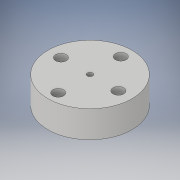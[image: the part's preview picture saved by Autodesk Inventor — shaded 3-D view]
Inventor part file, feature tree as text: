
AUTODESK INVENTOR PART (.ipt)
format: ipt  version: 2019 (Build 230136000, 136)  size: 108,544 bytes
history: native  units: mm
features: extrude x1, sketch x1
ambient origin geometry x8: Origin, YZ Plane, XZ Plane, XY Plane, X Axis, Y Axis, Z Axis, Center Point
bodies: Solid1 (feature_tree)
feature tree (2):
  extrude  "Extrusion1"  Depth=5.0mm
  sketch  "Sketch1"  dims[d0=78.0mm d1=5.0mm d2=10.0mm d3=10.0mm d4=10.0mm d5=10.0mm d6=25.0mm d7=0.0mm]
